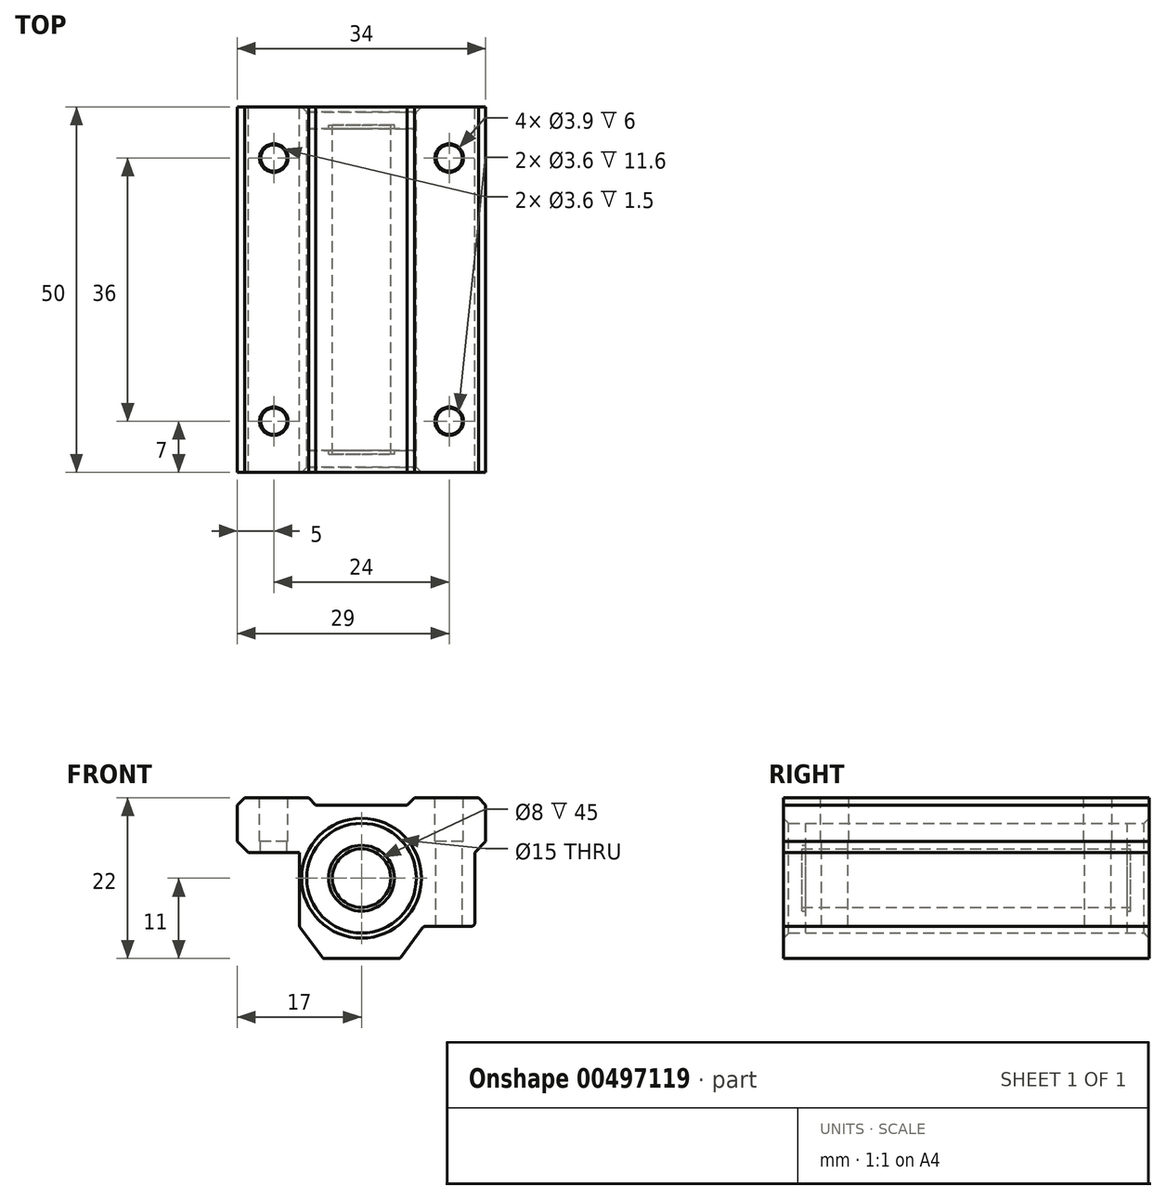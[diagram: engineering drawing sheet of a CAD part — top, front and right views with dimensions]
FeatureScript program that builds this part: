
annotation { "Feature Type Name" : "Feature", "Feature Type Description" : "" }
export const myFeature = defineFeature(function(context is Context, id is Id, definition is map)
    precondition{}
    {
        {
            var Q0;
            Q0=qCreatedBy(makeId("Front.planeOp"),FACE);
            var sketch = newSketch(context, id + "F0", { "sketchPlane" : qUnion([Q0])});
            skCircle(sketch, "E0", {"center": v(0, 0) * mm, "radius": 4 * mm});
            skCircle(sketch, "E1", {"center": v(0, 0) * mm, "radius": 7.5 * mm});
            skLineSegment(sketch, "E2", {"start": v(0, 0) * mm, "end": v(0, 22.9) * mm, "construction": true});
            skLineSegment(sketch, "E3", {"start": v(0, 7.5) * mm, "end": v(0, 10) * mm});
            skLineSegment(sketch, "E4", {"start": v(0, 10) * mm, "end": v(7.25, 10) * mm});
            skLineSegment(sketch, "E5", {"start": v(7.25, 10) * mm, "end": v(7.25, 11) * mm});
            skLineSegment(sketch, "E6", {"start": v(7.25, 11) * mm, "end": v(17, 11) * mm});
            skLineSegment(sketch, "E7", {"start": v(17, 11) * mm, "end": v(17, 3.5) * mm});
            skLineSegment(sketch, "E8", {"start": v(17, 3.5) * mm, "end": v(15.5, 3.5) * mm});
            skLineSegment(sketch, "E9", {"start": v(15.5, 3.5) * mm, "end": v(15.5, -6.6) * mm});
            skLineSegment(sketch, "E10", {"start": v(15.5, -6.6) * mm, "end": v(8.5, -6.6) * mm});
            skLineSegment(sketch, "E11", {"start": v(8.5, -6.6) * mm, "end": v(5.25, -11) * mm});
            skLineSegment(sketch, "E12", {"start": v(5.25, -11) * mm, "end": v(0, -11) * mm});
            skLineSegment(sketch, "E13", {"start": v(0, -11) * mm, "end": v(0, -7.5) * mm});
            skCircle(sketch, "E14", {"center": v(0, 0) * mm, "radius": 4.5 * mm});
            skLineSegment(sketch, "E15.MirrorCS", {"start": v(-5.25, -11) * mm, "end": v(0, -11) * mm});
            skLineSegment(sketch, "E16.MirrorCS", {"start": v(-8.5, -6.6) * mm, "end": v(-5.25, -11) * mm});
            skLineSegment(sketch, "E17.MirrorCS", {"start": v(-17, 3.5) * mm, "end": v(-15.5, 3.5) * mm});
            skLineSegment(sketch, "E18.MirrorCS", {"start": v(-17, 11) * mm, "end": v(-17, 3.5) * mm});
            skLineSegment(sketch, "E19.MirrorCS", {"start": v(-7.25, 11) * mm, "end": v(-17, 11) * mm});
            skLineSegment(sketch, "E20.MirrorCS", {"start": v(-7.25, 10) * mm, "end": v(-7.25, 11) * mm});
            skLineSegment(sketch, "E21.MirrorCS", {"start": v(0, 10) * mm, "end": v(-7.25, 10) * mm});
            skLineSegment(sketch, "E22", {"start": v(-8.5, -6.6) * mm, "end": v(-8.5, 3.5) * mm});
            skLineSegment(sketch, "E23", {"start": v(-8.5, 3.5) * mm, "end": v(-15.5, 3.5) * mm});
            skSolve(sketch);
        }
        {
            var Q0;
            {var subQ0=sQuery(id+"F0.wireOp",EDGE,"E3");Q0=makeQuery(id+"F0.imprint","IMPRINT",FACE,{"disambiguationData":[TD([[makeQuery(id+"F0.imprint","IMPRINT",EDGE,{"derivedFrom":subQ0}),-1.0]])]});}
            var Q1;
            {var subQ0=sQuery(id+"F0.wireOp",EDGE,"E3");Q1=makeQuery(id+"F0.imprint","IMPRINT",FACE,{"disambiguationData":[TD([[makeQuery(id+"F0.imprint","IMPRINT",EDGE,{"derivedFrom":subQ0}),1.0]])]});}
            extrude(context, id + "F1", {"entities" : qUnion([Q0, Q1]), "depth" : 50 * mm, "symmetric" : true});
        }
        {
            var Q0;
            Q0=makeQuery(id+"F1.opExtrude","SWEPT_EDGE",EDGE,{"disambiguationData":[OSD([sQuery(id+"F0.wireOp",EDGE,"E4"),sQuery(id+"F0.wireOp",EDGE,"E5")])]});
            var Q1;
            Q1=makeQuery(id+"F1.opExtrude","SWEPT_EDGE",EDGE,{"disambiguationData":[OSD([sQuery(id+"F0.wireOp",EDGE,"E6"),sQuery(id+"F0.wireOp",EDGE,"E7")])]});
            var Q2;
            Q2=makeQuery(id+"F1.opExtrude","SWEPT_EDGE",EDGE,{"disambiguationData":[OSD([sQuery(id+"F0.wireOp",EDGE,"E20.MirrorCS"),sQuery(id+"F0.wireOp",EDGE,"E21.MirrorCS")])]});
            var Q3;
            Q3=makeQuery(id+"F1.opExtrude","SWEPT_EDGE",EDGE,{"disambiguationData":[OSD([sQuery(id+"F0.wireOp",EDGE,"E18.MirrorCS"),sQuery(id+"F0.wireOp",EDGE,"E19.MirrorCS")])]});
            chamfer(context, id + "F2", {"entities" : qUnion([Q0, Q1, Q2, Q3]), "width" : 1 * mm, "tangentPropagation" : true});
        }
        {
            var Q0;
            Q0=makeQuery(id+"F1.opExtrude","SWEPT_EDGE",EDGE,{"disambiguationData":[OSD([sQuery(id+"F0.wireOp",EDGE,"E7"),sQuery(id+"F0.wireOp",EDGE,"E8")])]});
            var Q1;
            Q1=makeQuery(id+"F1.opExtrude","SWEPT_EDGE",EDGE,{"disambiguationData":[OSD([sQuery(id+"F0.wireOp",EDGE,"E17.MirrorCS"),sQuery(id+"F0.wireOp",EDGE,"E18.MirrorCS")])]});
            chamfer(context, id + "F3", {"entities" : qUnion([Q0, Q1]), "width" : 1.5 * mm, "tangentPropagation" : true});
        }
        {
            var Q0;
            Q0=makeQuery(id+"F1.opExtrude","SWEPT_EDGE",EDGE,{"disambiguationData":[OSD([sQuery(id+"F0.wireOp",EDGE,"E9"),sQuery(id+"F0.wireOp",EDGE,"E10")])]});
            var Q1;
            Q1=makeQuery(id+"F1.opExtrude","SWEPT_EDGE",EDGE,{"disambiguationData":[OSD([sQuery(id+"F0.wireOp",EDGE,"E10"),sQuery(id+"F0.wireOp",EDGE,"E11")])]});
            var Q2;
            Q2=makeQuery(id+"F1.opExtrude","SWEPT_EDGE",EDGE,{"disambiguationData":[OSD([sQuery(id+"F0.wireOp",EDGE,"E11"),sQuery(id+"F0.wireOp",EDGE,"E12")])]});
            var Q3;
            Q3=makeQuery(id+"F1.opExtrude","SWEPT_EDGE",EDGE,{"disambiguationData":[OSD([sQuery(id+"F0.wireOp",EDGE,"E15.MirrorCS"),sQuery(id+"F0.wireOp",EDGE,"E16.MirrorCS")])]});
            var Q4;
            Q4=makeQuery(id+"F1.opExtrude","SWEPT_EDGE",EDGE,{"disambiguationData":[OSD([sQuery(id+"F0.wireOp",EDGE,"E16.MirrorCS"),sQuery(id+"F0.wireOp",EDGE,"E22")])]});
            fillet(context, id + "F4", {"entities" : qUnion([Q0, Q1, Q2, Q3, Q4]), "radius" : .5 * mm, "tangentPropagation" : true, "allowEdgeOverflow" : false});
        }
        {
            var Q0;
            Q0=makeQuery(id+"F1.opExtrude","SWEPT_FACE",FACE,{"disambiguationData":[OSD([sQuery(id+"F0.wireOp",EDGE,"E6")])]});
            var sketch = newSketch(context, id + "F5", { "sketchPlane" : qUnion([Q0])});
            skLineSegment(sketch, "E24.bottom", {"start": v(-12, 18) * mm, "end": v(12, 18) * mm});
            skLineSegment(sketch, "E24.top", {"start": v(-12, -18) * mm, "end": v(12, -18) * mm});
            skLineSegment(sketch, "E24.left", {"start": v(-12, 18) * mm, "end": v(-12, -18) * mm});
            skLineSegment(sketch, "E24.right", {"start": v(12, 18) * mm, "end": v(12, -18) * mm});
            skLineSegment(sketch, "E25", {"start": v(-12, 18) * mm, "end": v(12, -18) * mm});
            skSolve(sketch);
        }
        {
            var Q0;
            Q0=sQuery(id+"F5.wireOp",VERTEX,"E24.right.start");
            var Q1;
            Q1=sQuery(id+"F5.wireOp",VERTEX,"E25.end");
            var Q2;
            Q2=sQuery(id+"F5.wireOp",VERTEX,"E25.start");
            var Q3;
            Q3=sQuery(id+"F5.wireOp",VERTEX,"E24.left.end");
            var Q4;
            Q4=makeQuery(id+"F1.opExtrude","SWEPT_BODY",BODY,{"disambiguationData":[OSD([sQuery(id+"F0.wireOp",EDGE,"E1"),sQuery(id+"F0.wireOp",EDGE,"E3"),sQuery(id+"F0.wireOp",EDGE,"E4"),sQuery(id+"F0.wireOp",EDGE,"E5"),sQuery(id+"F0.wireOp",EDGE,"E6"),sQuery(id+"F0.wireOp",EDGE,"E7"),sQuery(id+"F0.wireOp",EDGE,"E8"),sQuery(id+"F0.wireOp",EDGE,"E9"),sQuery(id+"F0.wireOp",EDGE,"E10"),sQuery(id+"F0.wireOp",EDGE,"E11"),sQuery(id+"F0.wireOp",EDGE,"E12"),sQuery(id+"F0.wireOp",EDGE,"E13")])]});
            hole(context, id + "F6", {"style" : HoleStyle.C_BORE, "endStyle" : HoleEndStyle.THROUGH, "holeDiameter" : 3.6 * mm, "cBoreDiameter" : 3.9 * mm, "cBoreDepth" : 6 * mm, "locations" : qUnion([Q0, Q1, Q2, Q3]), "scope" : qUnion([Q4]), "tappedDepth" : 12 * mm, "tapClearance" : 3});
        }
        {
            var Q0;
            Q0=makeQuery(id+"F6.hole-1.boolean.opBoolean","COPY",EDGE,{"derivedFrom":makeQuery(id+"F6.hole-1.opRevolve","SWEPT_EDGE",EDGE,{"disambiguationData":[OSD([sQuery(id+"F6.hole-1.sketch.wireOp",EDGE,"cbore_start_line_2"),sQuery(id+"F6.hole-1.sketch.wireOp",EDGE,"cbore_start_line_3")])]})});
            var Q1;
            Q1=makeQuery(id+"F6.hole-0.boolean.opBoolean","COPY",EDGE,{"derivedFrom":makeQuery(id+"F6.hole-0.opRevolve","SWEPT_EDGE",EDGE,{"disambiguationData":[OSD([sQuery(id+"F6.hole-0.sketch.wireOp",EDGE,"cbore_start_line_2"),sQuery(id+"F6.hole-0.sketch.wireOp",EDGE,"cbore_start_line_3")])]})});
            var Q2;
            Q2=makeQuery(id+"F1.opExtrude","CAP_EDGE",EDGE,{"disambiguationData":[OSD([sQuery(id+"F0.wireOp",EDGE,"E1")])],"isStart":false});
            var Q3;
            Q3=makeQuery(id+"F1.opExtrude","CAP_EDGE",EDGE,{"disambiguationData":[OSD([sQuery(id+"F0.wireOp",EDGE,"E1")])],"isStart":true});
            var Q4;
            Q4=makeQuery(id+"F6.hole-3.boolean.opBoolean","COPY",EDGE,{"derivedFrom":makeQuery(id+"F6.hole-3.opRevolve","SWEPT_EDGE",EDGE,{"disambiguationData":[OSD([sQuery(id+"F6.hole-3.sketch.wireOp",EDGE,"cbore_start_line_2"),sQuery(id+"F6.hole-3.sketch.wireOp",EDGE,"cbore_start_line_3")])]})});
            var Q5;
            Q5=makeQuery(id+"F6.hole-2.boolean.opBoolean","COPY",EDGE,{"derivedFrom":makeQuery(id+"F6.hole-2.opRevolve","SWEPT_EDGE",EDGE,{"disambiguationData":[OSD([sQuery(id+"F6.hole-2.sketch.wireOp",EDGE,"cbore_start_line_2"),sQuery(id+"F6.hole-2.sketch.wireOp",EDGE,"cbore_start_line_3")])]})});
            chamfer(context, id + "F7", {"entities" : qUnion([Q0, Q1, Q2, Q3, Q4, Q5]), "width" : .7 * mm, "tangentPropagation" : true});
        }
        {
            var Q0;
            Q0=makeQuery(id+"F0.imprint","IMPRINT",FACE,{"disambiguationData":[TD([[makeQuery(id+"F0.imprint","IMPRINT",EDGE,{"derivedFrom":sQuery(id+"F0.wireOp",EDGE,"E14")}),-1.0]])]});
            extrude(context, id + "F8", {"entities" : qUnion([Q0]), "depth" : 44 * mm, "symmetric" : true});
        }
        {
            var Q0;
            Q0=makeQuery(id+"F0.imprint","IMPRINT",FACE,{"disambiguationData":[TD([[makeQuery(id+"F0.imprint","IMPRINT",EDGE,{"derivedFrom":sQuery(id+"F0.wireOp",EDGE,"E0")}),-1.0]])]});
            extrude(context, id + "F9", {"entities" : qUnion([Q0]), "operationType" : NewBodyOperationType.ADD, "depth" : 45 * mm, "symmetric" : true});
        }
    });
